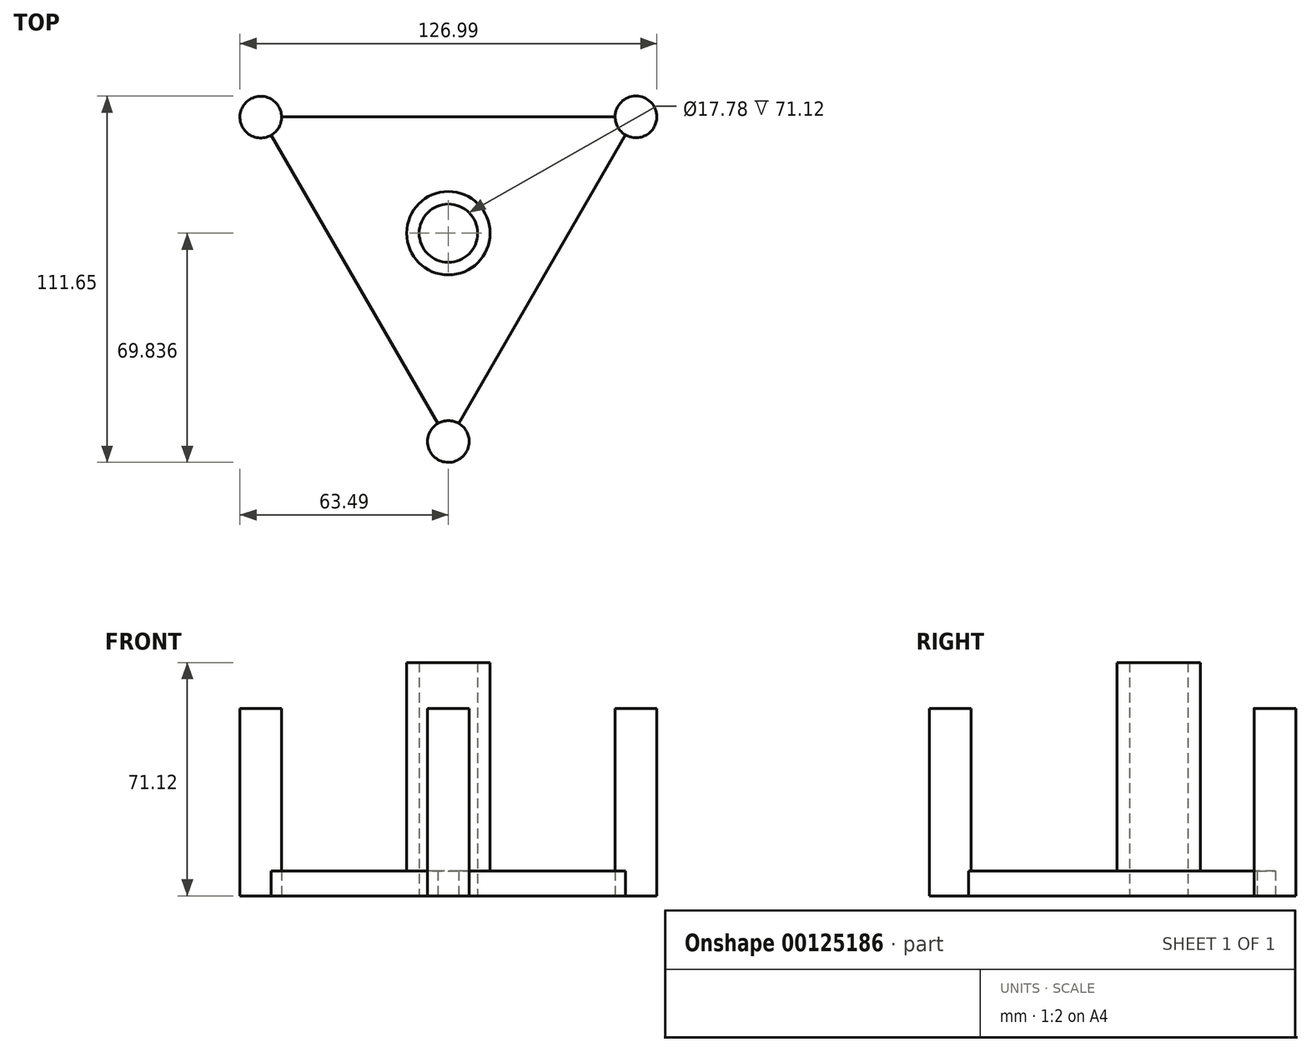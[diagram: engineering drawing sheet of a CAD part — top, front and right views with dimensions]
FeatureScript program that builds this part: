
annotation { "Feature Type Name" : "Feature", "Feature Type Description" : "" }
export const myFeature = defineFeature(function(context is Context, id is Id, definition is map)
    precondition{}
    {
        {
            var Q0;
            Q0=qCreatedBy(makeId("Top.planeOp"),FACE);
            var sketch = newSketch(context, id + "F0", { "sketchPlane" : qUnion([Q0])});
            skLineSegment(sketch, "E0", {"start": v(0, -48.51) * mm, "end": v(-57.15, 50.47) * mm});
            skLineSegment(sketch, "E1", {"start": v(-57.15, 50.47) * mm, "end": v(57.15, 50.47) * mm});
            skLineSegment(sketch, "E2", {"start": v(57.15, 50.47) * mm, "end": v(0, -48.51) * mm});
            skPoint(sketch, "E3.center.orphan", {"position": v(0, 14.99) * mm});
            skSolve(sketch);
        }
        {
            var Q0;
            Q0 = qSketchRegion(id + "F0", true);
            extrude(context, id + "F1", {"entities" : qUnion([Q0]), "depth" : 7.62 * mm});
        }
        {
            var Q0;
            Q0=makeQuery(id+"F1.opExtrude","CAP_FACE",FACE,{"disambiguationData":[OSD([sQuery(id+"F0.wireOp",EDGE,"E0"),sQuery(id+"F0.wireOp",EDGE,"E1"),sQuery(id+"F0.wireOp",EDGE,"E2")])],"isStart":false});
            var sketch = newSketch(context, id + "F2", { "sketchPlane" : qUnion([Q0])});
            skCircle(sketch, "E4", {"center": v(0, 14.99) * mm, "radius": 12.7 * mm});
            skSolve(sketch);
        }
        {
            var Q0;
            Q0 = qSketchRegion(id + "F2", true);
            extrude(context, id + "F3", {"entities" : qUnion([Q0]), "operationType" : NewBodyOperationType.ADD, "depth" : 63.5 * mm});
        }
        {
            var Q0;
            Q0=qCreatedBy(makeId("Top.planeOp"),FACE);
            var sketch = newSketch(context, id + "F4", { "sketchPlane" : qUnion([Q0])});
            skCircle(sketch, "E5", {"center": v(0, 14.99) * mm, "radius": 8.9 * mm});
            skSolve(sketch);
        }
        {
            var Q0;
            Q0 = qSketchRegion(id + "F4", true);
            extrude(context, id + "F5", {"entities" : qUnion([Q0]), "operationType" : NewBodyOperationType.REMOVE, "endBound" : BoundingType.THROUGH_ALL, "depth" : 25.4 * mm});
        }
        {
            var Q0;
            Q0=qCreatedBy(makeId("Top.planeOp"),FACE);
            var sketch = newSketch(context, id + "F6", { "sketchPlane" : qUnion([Q0])});
            skCircle(sketch, "E6", {"center": v(0, -48.5) * mm, "radius": 6.35 * mm});
            skCircle(sketch, "E7", {"center": v(-57.14, 50.38) * mm, "radius": 6.35 * mm});
            skCircle(sketch, "E8", {"center": v(57.15, 50.45) * mm, "radius": 6.35 * mm});
            skSolve(sketch);
        }
        {
            var Q0;
            Q0 = qSketchRegion(id + "F6", true);
            extrude(context, id + "F7", {"entities" : qUnion([Q0]), "operationType" : NewBodyOperationType.ADD, "depth" : 57.15 * mm});
        }
    });
